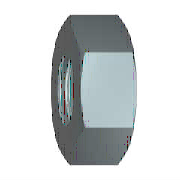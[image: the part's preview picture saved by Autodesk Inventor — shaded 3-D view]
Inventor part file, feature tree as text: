
AUTODESK INVENTOR PART (.ipt)
format: ipt  version: 2023 (Build 270158000, 158)  size: 164,864 bytes
history: native  units: mm (DEFAULTED — no unit token found)
features: sketch x3, other x2, extrude x1, hole x1, plane x1
ambient origin geometry x7: Origin, YZ Plane, XZ Plane, X Axis, Y Axis, Z Axis, Center Point
bodies: Solid1 (feature_tree)
feature tree (8):
  extrude  "Базовый элемент"  Depth=20.78461mm
  other  "Фаска1"
  hole  "Резьба"  [1 undecoded]
  other  "Work Axis1"
  plane  "Work Plane1"
  sketch  "Эскиз1"
  sketch  "Эскиз2"
  sketch  "Эскиз3"
note: 1 required parameter value undecoded (feature->parameter linkage not recoverable at this tier; creation-order binding heuristic only, values carry confidence <= 0.55)
